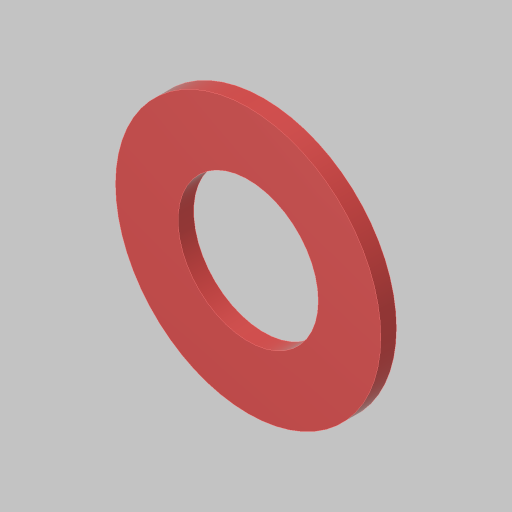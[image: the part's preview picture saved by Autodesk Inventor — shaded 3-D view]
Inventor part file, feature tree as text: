
AUTODESK INVENTOR PART (.ipt)
format: ipt  version: 2023.5 (Build 275446000, 446)  size: 97,792 bytes
history: native  units: in
note: dims shown in document units (in); Inventor stores cm internally (conversion verified against a paired STEP export)
features: extrude x1, sketch x1
ambient origin geometry x8: Origin, YZ Plane, XZ Plane, XY Plane, X Axis, Y Axis, Z Axis, Center Point
bodies: Solid1 (feature_tree)
feature tree (2):
  extrude  "Extrusion1"  Depth=0.0625in
  sketch  "Sketch1"  dims[d0=0.56in d1=0.25in d2=0.0625in d3=0.0in]
